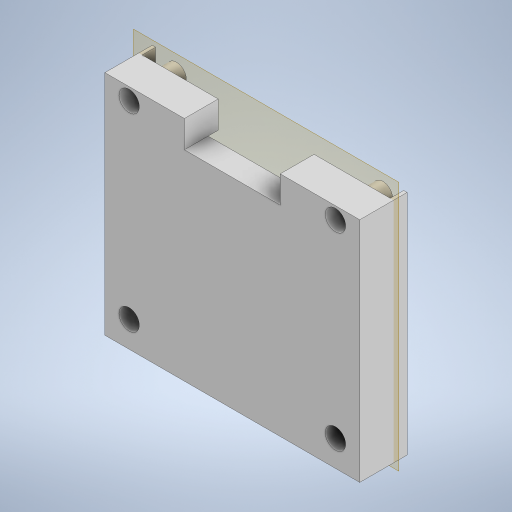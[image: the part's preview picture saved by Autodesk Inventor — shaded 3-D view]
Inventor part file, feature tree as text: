
AUTODESK INVENTOR PART (.ipt)
format: ipt  version: 2024.3 (Build 283343000, 343)  size: 291,840 bytes
history: native  units: in
note: dims shown in document units (in); Inventor stores cm internally (conversion verified against a paired STEP export)
features: reference x11, extrude x6, sketch x6, other x4, plane x1
ambient origin geometry x8: Origin, YZ Plane, XZ Plane, XY Plane, X Axis, Y Axis, Z Axis, Center Point
bodies: Solid1 (feature_tree)
feature tree (28):
  plane  "Work Plane1"
  extrude  "Extrusion1"  Depth=0.0394in
  extrude  "Extrusion2"  Depth=0.0394in
  extrude  "Extrusion3"  Depth=0.1969in
  extrude  "Extrusion4"  Depth=0.1181in TaperAngle=0.0deg
  extrude  "Extrusion5"  Depth=0.0787in TaperAngle=0.0deg
  extrude  "Extrusion6"  Depth=0.0197in
  sketch  "Sketch1"  dims[d0=0.0394in d1=0.0394in]
  reference  "Reference1"
  reference  "Reference2"
  reference  "Reference3"
  sketch  "Sketch2"  dims[d2=0.0394in d3=0.0394in]
  reference  "Reference4"
  reference  "Reference5"
  reference  "Reference6"
  reference  "Reference7"
  sketch  "Sketch3"  dims[d4=0.0787in d5=0.1969in]
  reference  "Reference8"
  reference  "Reference9"
  reference  "Reference10"
  reference  "Reference11"
  sketch  "Sketch4"  dims[d6=0.1969in d7=0.0in d8=0.1181in d9=0.0in]
  sketch  "Sketch5"  dims[d10=0.1142in d11=0.0787in d12=0.0in]
  sketch  "Sketch6"  dims[d13=0.0197in d14=0.0197in d15=0.0197in d16=0.0197in d17=0.0787in d18=0.0in d19=0.0787in d20=0.0in d21=0.0394in d22=0.0394in d23=0.1181in d24=0.0591in d25=0.0in]
  other  "<userpath>\Dropbox\elec\Mechanical\DCBuddyV2\OLED_With_Carrier.iam"
  other  "OLED_With_Carrier.iam"
  other  "User Library-OLED-1_3-128X64:1"
  other  "User Library-OLED-1_3-128X64_1"
